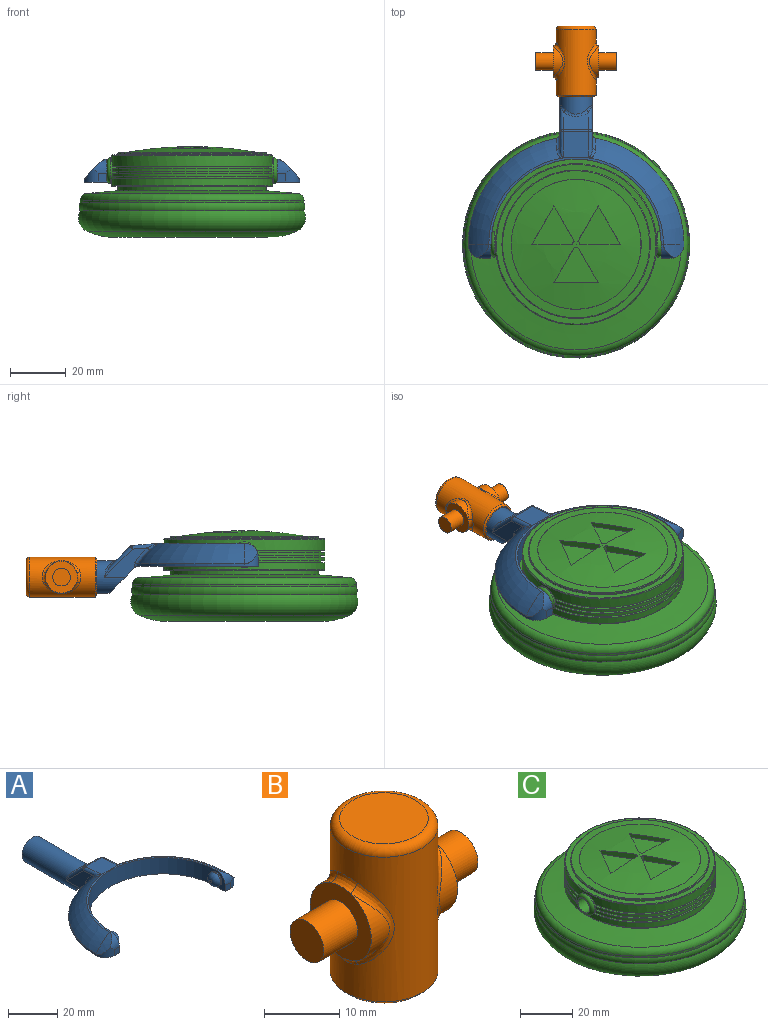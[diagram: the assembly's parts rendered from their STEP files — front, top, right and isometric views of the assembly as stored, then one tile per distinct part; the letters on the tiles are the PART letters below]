
ASSEMBLY  parts=3 mates=2
PART A: 48 faces, bbox 77.3x80.8x18.2 mm
  f0: plane 11.99x9.83mm, normal (0,-0.71,-0.71), area 141.5mm2, adj f1,f2,f9,f30,f43,f46
  f1: plane 15.39x10.49mm, normal (-1,0,0), area 63.5mm2, adj f0,f30,f32,f36,f46,f47
  f2: plane 15.39x10.49mm, normal (1,0,0), area 63.5mm2, adj f0,f30,f34,f39,f43,f44
  f3: plane 9.14x6.37mm, normal (0,0.71,0.71), area 67.6mm2, adj f35,f36,f39,f40
  f4: cylinder r=38.61mm len=37.99mm, axis (0,0,-1), area 42.6mm2, adj f6,f9,f17,f46,f47
  f5: torus R=19.3mm, axis (0,0,-1), area 507.8mm2, adj f10,f11,f12,f29,f42,f44
  f6: torus R=19.3mm, axis (0,0,-1), area 507.8mm2, adj f4,f11,f15,f28,f45,f47
  f7: cylinder r=30.48mm len=60.96mm, axis (0,0,-1), area 746.6mm2, adj f8,f9,f11,f14,f21,f24
  f8: plane 8.13x5.08mm, normal (-1,0,0), area 19.9mm2, adj f7,f9,f13,f19,f24
  f9: plane 77.22x43.73mm, normal (0,0,-1), area 956.2mm2, adj f0,f4,f7,f8,f10,f13,f14,f16
  f10: cylinder r=38.61mm len=37.99mm, axis (0,0,-1), area 42.6mm2, adj f5,f9,f20,f43,f44
  f11: plane 62.55x30.95mm, normal (0,0,1), area 75mm2, adj f5,f6,f7,f18,f19,f27
  f12: cylinder r=22.71mm len=7.33mm, axis (0,1,0), area 24.8mm2, adj f5,f19,f20
  f13: plane 3.05x3.05mm, normal (0,-1,0), area 9.3mm2, adj f8,f9,f19,f20
  f14: plane 8.13x5.08mm, normal (1,0,0), area 19.9mm2, adj f7,f9,f16,f18,f21
  f15: cylinder r=22.71mm len=7.33mm, axis (0,1,0), area 24.8mm2, adj f6,f17,f18
  f16: plane 3.05x3.05mm, normal (0,-1,0), area 9.3mm2, adj f9,f14,f17,f18
  f17: cylinder r=5.08mm len=5.08mm, axis (0,0,-1), area 21.9mm2, adj f4,f9,f15,f16,f18
  f18: cylinder r=5.08mm len=5.08mm, axis (-1,0,0), area 21.9mm2, adj f11,f14,f15,f16,f17
  f19: cylinder r=5.08mm len=5.08mm, axis (-1,0,0), area 21.9mm2, adj f8,f11,f12,f13,f20
  f20: cylinder r=5.08mm len=5.08mm, axis (0,0,-1), area 21.9mm2, adj f9,f10,f12,f13,f19
  f21: cylinder r=3.17mm len=6.35mm, axis (-1,0,0), area 12.7mm2, adj f7,f14,f23
  f22: plane 1.27x1.27mm, normal (1,0,0), area 1.3mm2, adj f23
  f23: torus R=0.64mm, axis (1,0,0), area 56.5mm2, adj f21,f22
  f24: cylinder r=3.17mm len=6.35mm, axis (1,0,0), area 12.7mm2, adj f7,f8,f26
  f25: plane 1.27x1.27mm, normal (-1,0,0), area 1.3mm2, adj f26
  f26: torus R=0.64mm, axis (-1,0,0), area 56.5mm2, adj f24,f25
  f27: plane 9.86x9.36mm, normal (0,0.09,1), area 85.6mm2, adj f11,f28,f29,f32,f34,f35,f42,f45
  f28: plane 1.04x0.17mm, normal (0,-1,0), area 0mm2, adj f6,f27,f45
  f29: plane 1.04x0.17mm, normal (0,-1,0), area 0mm2, adj f5,f27,f42
  f30: cylinder r=5.84mm len=33.01mm, axis (0,-1,0), area 1029.7mm2, adj f0,f1,f2,f31,f38,f40,f41
  f31: plane 11.68x11.68mm, normal (0,1,0), area 107.2mm2, adj f30
  f32: cylinder r=1.27mm len=9.13mm, axis (0,-1,0.09), area 14.4mm2, adj f1,f27,f33,f45
  f33: sphere r=1.27mm, area 1.5mm2, adj f32,f35,f36
  f34: cylinder r=1.27mm len=9.13mm, axis (0,1,-0.09), area 14.4mm2, adj f2,f27,f37,f42
  f35: cylinder r=1.27mm len=9.14mm, axis (-1,0,0), area 8.1mm2, adj f3,f27,f33,f37
  f36: cylinder r=1.27mm len=10.91mm, axis (0,-0.71,0.71), area 23.1mm2, adj f1,f3,f33,f38
  f37: sphere r=1.27mm, area 1.5mm2, adj f34,f35,f39
  f38: bspline ~4.55x2.75mm, area 2.3mm2, adj f30,f36,f40
  f39: cylinder r=1.27mm len=10.91mm, axis (0,0.71,-0.71), area 23.1mm2, adj f2,f3,f37,f41
  f40: bspline ~9.14x2.56mm, area 10.7mm2, adj f3,f30,f38,f41
  f41: bspline ~5.23x3.53mm, area 2.3mm2, adj f30,f39,f40
  f42: bspline ~4.62x3.14mm, area 5.2mm2, adj f5,f27,f29,f34,f44
  f43: cylinder r=1.27mm len=1.74mm, axis (0,0,-1), area 1.9mm2, adj f0,f2,f9,f10,f44
  f44: bspline ~8.6x7.86mm, area 11.9mm2, adj f2,f5,f10,f42,f43
  f45: bspline ~4.62x3.14mm, area 5.2mm2, adj f6,f27,f28,f32,f47
  f46: cylinder r=1.27mm len=1.74mm, axis (0,0,-1), area 1.9mm2, adj f0,f1,f4,f9,f47
  f47: bspline ~8.6x7.86mm, area 11.9mm2, adj f1,f4,f6,f45,f46
PART B: 25 faces, bbox 28.9x15.5x25.4 mm
  f0: cylinder r=5.71mm len=10.81mm, axis (-1,0,0), area 26.2mm2, adj f5,f15
  f1: cylinder r=5.71mm len=10.81mm, axis (-1,0,0), area 26.2mm2, adj f8,f11
  f2: cylinder r=7.14mm len=23.5mm, axis (0,0,-1), area 763.2mm2, adj f9,f10,f11,f12,f13,f14,f15,f16
  f3: plane 11.75x11.75mm, normal (0,0,1), area 108.4mm2, adj f17
  f4: plane 13.02x13.02mm, normal (0,0,-1), area 16.3mm2, adj f22,f24
  f5: plane 11.46x11.46mm, normal (1,0,0), area 70.9mm2, adj f0,f6,f13,f16,f18
  f6: cylinder r=5.71mm len=10.81mm, axis (-1,0,0), area 26.2mm2, adj f5,f14
  f7: cylinder r=5.71mm len=10.81mm, axis (-1,0,0), area 26.2mm2, adj f8,f10
  f8: plane 11.46x11.46mm, normal (-1,0,0), area 70.9mm2, adj f1,f7,f9,f12,f20
  f9: bspline ~4.64x1.73mm, area 6.5mm2, adj f2,f8,f10,f11
  f10: bspline ~13.62x4.91mm, area 20.7mm2, adj f2,f7,f9,f12
  f11: bspline ~13.6x4.87mm, area 20.7mm2, adj f1,f2,f9,f12
  f12: bspline ~4.64x1.73mm, area 6.5mm2, adj f2,f8,f10,f11
  f13: bspline ~4.64x1.73mm, area 6.5mm2, adj f2,f5,f14,f15
  f14: bspline ~13.62x4.91mm, area 20.7mm2, adj f2,f6,f13,f16
  f15: bspline ~13.6x4.87mm, area 20.7mm2, adj f0,f2,f13,f16
  f16: bspline ~4.64x1.73mm, area 6.5mm2, adj f2,f5,f14,f15
  f17: torus R=5.87mm, axis (0,0,1), area 83.8mm2, adj f2,f3
  f18: cylinder r=3.17mm len=6.35mm, axis (-1,0,0), area 126.7mm2, adj f5,f19
  f19: plane 6.35x6.35mm, normal (1,0,0), area 31.7mm2, adj f18
  f20: cylinder r=3.17mm len=6.35mm, axis (1,0,0), area 126.7mm2, adj f8,f21
  f21: plane 6.35x6.35mm, normal (-1,0,0), area 31.7mm2, adj f20
  f22: cylinder r=6.1mm len=22.86mm, axis (0,0,-1), area 875.6mm2, adj f4,f23
  f23: plane 12.19x12.19mm, normal (0,0,-1), area 116.7mm2, adj f22
  f24: cone r=7.14mm half-angle=45deg, axis (0,0,1), area 38.5mm2, adj f2,f4
PART C: 64 faces, bbox 96.3x96.3x32.5 mm
  f0: cylinder r=28.87mm len=57.73mm, axis (0,0,-1), area 433.8mm2, adj f1,f2,f54,f55,f60
  f1: plane 57.3x25.32mm, normal (0,0,1), area 103.6mm2, adj f0,f4,f54,f55
  f2: plane 57.3x25.32mm, normal (0,0,1), area 103.6mm2, adj f0,f3,f54,f55
  f3: cylinder r=27.6mm len=54.74mm, axis (0,0,1), area 50.3mm2, adj f2,f6,f54,f55
  f4: cylinder r=27.6mm len=54.74mm, axis (0,0,1), area 50.3mm2, adj f1,f5,f54,f55
  f5: plane 57.18x24.89mm, normal (0,0,-1), area 102.5mm2, adj f4,f7,f54,f55
  f6: plane 57.18x24.89mm, normal (0,0,-1), area 102.5mm2, adj f3,f8,f54,f55
  f7: cylinder r=28.87mm len=57.18mm, axis (0,0,-1), area 104.3mm2, adj f5,f9,f54,f55
  f8: cylinder r=28.87mm len=57.18mm, axis (0,0,-1), area 104.3mm2, adj f6,f10,f54,f55
  f9: plane 57.04x24.4mm, normal (0,0,1), area 101.2mm2, adj f7,f12,f54,f55
  f10: plane 57.04x24.4mm, normal (0,0,1), area 101.2mm2, adj f8,f11,f54,f55
  f11: cylinder r=27.6mm len=54.47mm, axis (0,0,1), area 49.3mm2, adj f10,f14,f54,f55
  f12: cylinder r=27.6mm len=54.47mm, axis (0,0,1), area 49.3mm2, adj f9,f13,f54,f55
  f13: plane 57.01x24.31mm, normal (0,0,-1), area 101mm2, adj f12,f15,f54,f55
  f14: plane 57.01x24.31mm, normal (0,0,-1), area 101mm2, adj f11,f16,f54,f55
  f15: cylinder r=28.87mm len=57.04mm, axis (0,0,-1), area 103.6mm2, adj f13,f17,f54,f55
  f16: cylinder r=28.87mm len=57.04mm, axis (0,0,-1), area 103.6mm2, adj f14,f18,f54,f55
  f17: plane 57.04x24.39mm, normal (0,0,1), area 101.2mm2, adj f15,f20,f54,f55
  f18: plane 57.04x24.39mm, normal (0,0,1), area 101.2mm2, adj f16,f19,f54,f55
  f19: cylinder r=27.6mm len=54.52mm, axis (0,0,1), area 49.5mm2, adj f18,f22,f54,f55
  f20: cylinder r=27.6mm len=54.52mm, axis (0,0,1), area 49.5mm2, adj f17,f21,f54,f55
  f21: plane 57.09x24.57mm, normal (0,0,-1), area 101.7mm2, adj f20,f23,f54,f55
  f22: plane 57.09x24.57mm, normal (0,0,-1), area 101.7mm2, adj f19,f23,f54,f55
  f23: cylinder r=28.87mm len=57.73mm, axis (0,0,-1), area 652mm2, adj f21,f22,f54,f55,f61
  f24: sphere r=135.39mm, area 1385.3mm2, adj f38,f39,f40,f41,f43,f44,f45,f46
  f25: plane 39.35x39.35mm, normal (0,0,-1), area 1216.2mm2, adj f26
  f26: torus R=20.13mm, axis (0,0,-1), area 1430.4mm2, adj f25,f27
  f27: torus R=27.75mm, axis (0,0,-1), area 3543.7mm2, adj f26,f28
  f28: torus R=35.37mm, axis (0,0,-1), area 2180.8mm2, adj f27,f29
  f29: torus R=37.36mm, axis (0,0,-1), area 734.8mm2, adj f28,f30
  f30: cylinder r=40.07mm len=80.14mm, axis (0,0,-1), area 213.4mm2, adj f29,f34
  f31: cone r=26.58mm half-angle=85deg, axis (0,0,-1), area 2265.9mm2, adj f32,f34
  f32: cylinder r=26.58mm len=53.16mm, axis (0,0,-1), area 265.1mm2, adj f31,f33
  f33: plane 57.23x57.23mm, normal (0,0,-1), area 352.3mm2, adj f32,f60
  f34: torus R=37.53mm, axis (0,0,1), area 928.9mm2, adj f30,f31
  f35: cone r=26.58mm half-angle=87deg, axis (0,0,-1), area 477.5mm2, adj f62,f63
  f36: cylinder r=26.58mm len=53.16mm, axis (0,0,-1), area 92.3mm2, adj f37,f62
  f37: plane 57.23x57.23mm, normal (0,0,1), area 352.3mm2, adj f36,f61
  f38: cylinder r=1.27mm len=2.53mm, axis (0,0,1), area 3.4mm2, adj f24,f39,f41,f42
  f39: plane 14.61x2.53mm, normal (0,1,0), area 32.2mm2, adj f24,f38,f40,f42
  f40: plane 13.75x7.94mm, normal (-0.87,-0.5,0), area 28mm2, adj f24,f39,f41,f42
  f41: plane 12.65x7.3mm, normal (0.87,-0.5,0), area 32.2mm2, adj f24,f38,f40,f42
  f42: plane 15.24x13.75mm, normal (0,0,1), area 108.3mm2, adj f38,f39,f40,f41
  f43: plane 12.65x7.3mm, normal (-0.87,-0.5,0), area 32.2mm2, adj f24,f44,f46,f47
  f44: cylinder r=1.27mm len=2.53mm, axis (0,0,1), area 3.4mm2, adj f24,f43,f45,f47
  f45: plane 12.65x7.3mm, normal (0.87,-0.5,0), area 32.2mm2, adj f24,f44,f46,f47
  f46: plane 15.88x1.84mm, normal (0,1,0), area 28mm2, adj f24,f43,f45,f47
  f47: plane 15.88x12.65mm, normal (0,0,1), area 108.3mm2, adj f43,f44,f45,f46
  f48: plane 12.65x7.3mm, normal (-0.87,-0.5,0), area 32.2mm2, adj f24,f49,f51,f52
  f49: plane 13.75x7.94mm, normal (0.87,-0.5,0), area 28mm2, adj f24,f48,f50,f52
  f50: plane 14.61x2.53mm, normal (0,1,0), area 32.2mm2, adj f24,f49,f51,f52
  f51: cylinder r=1.27mm len=2.53mm, axis (0,0,1), area 3.4mm2, adj f24,f48,f50,f52
  f52: plane 15.24x13.75mm, normal (0,0,1), area 108.3mm2, adj f48,f49,f50,f51
  f53: plane 6.6x6.6mm, normal (1,0,0), area 2.6mm2, adj f58,f59
  f54: cylinder r=4.57mm len=9.14mm, axis (-1,0,0), area 20.4mm2, adj f0,f1,f2,f3,f4,f5,f6,f7
  f55: cylinder r=4.57mm len=9.14mm, axis (-1,0,0), area 20.4mm2, adj f0,f1,f2,f3,f4,f5,f6,f7
  f56: plane 6.6x6.6mm, normal (-1,0,0), area 2.6mm2, adj f57,f59
  f57: torus R=3.3mm, axis (1,0,0), area 51.5mm2, adj f55,f56
  f58: torus R=3.3mm, axis (1,0,0), area 51.5mm2, adj f53,f54
  f59: cylinder r=3.17mm len=60.96mm, axis (1,0,0), area 1216.1mm2, adj f53,f56
  f60: torus R=28.61mm, axis (0,0,1), area 72.1mm2, adj f0,f33
  f61: torus R=28.61mm, axis (0,0,-1), area 72.1mm2, adj f23,f37
  f62: torus R=26.33mm, axis (0,0,1), area 64.2mm2, adj f35,f36
  f63: torus R=23.29mm, axis (0,0,1), area 4.5mm2, adj f24,f35
PLACE A t=(32.34,27.52,20.85)mm
PLACE B rot(axis=(-1,0,0),90deg) t=(32.34,80.3,16.88)mm
PLACE C t=(32.34,27.52,33.52)mm
MATE revolute A.f24 <-> C.f54  axis (-1,0,0) through (62.82,27.52,24.92)mm
MATE revolute B.f2 <-> A.f30  axis (0,-1,0) through (32.34,103.16,16.88)mm
